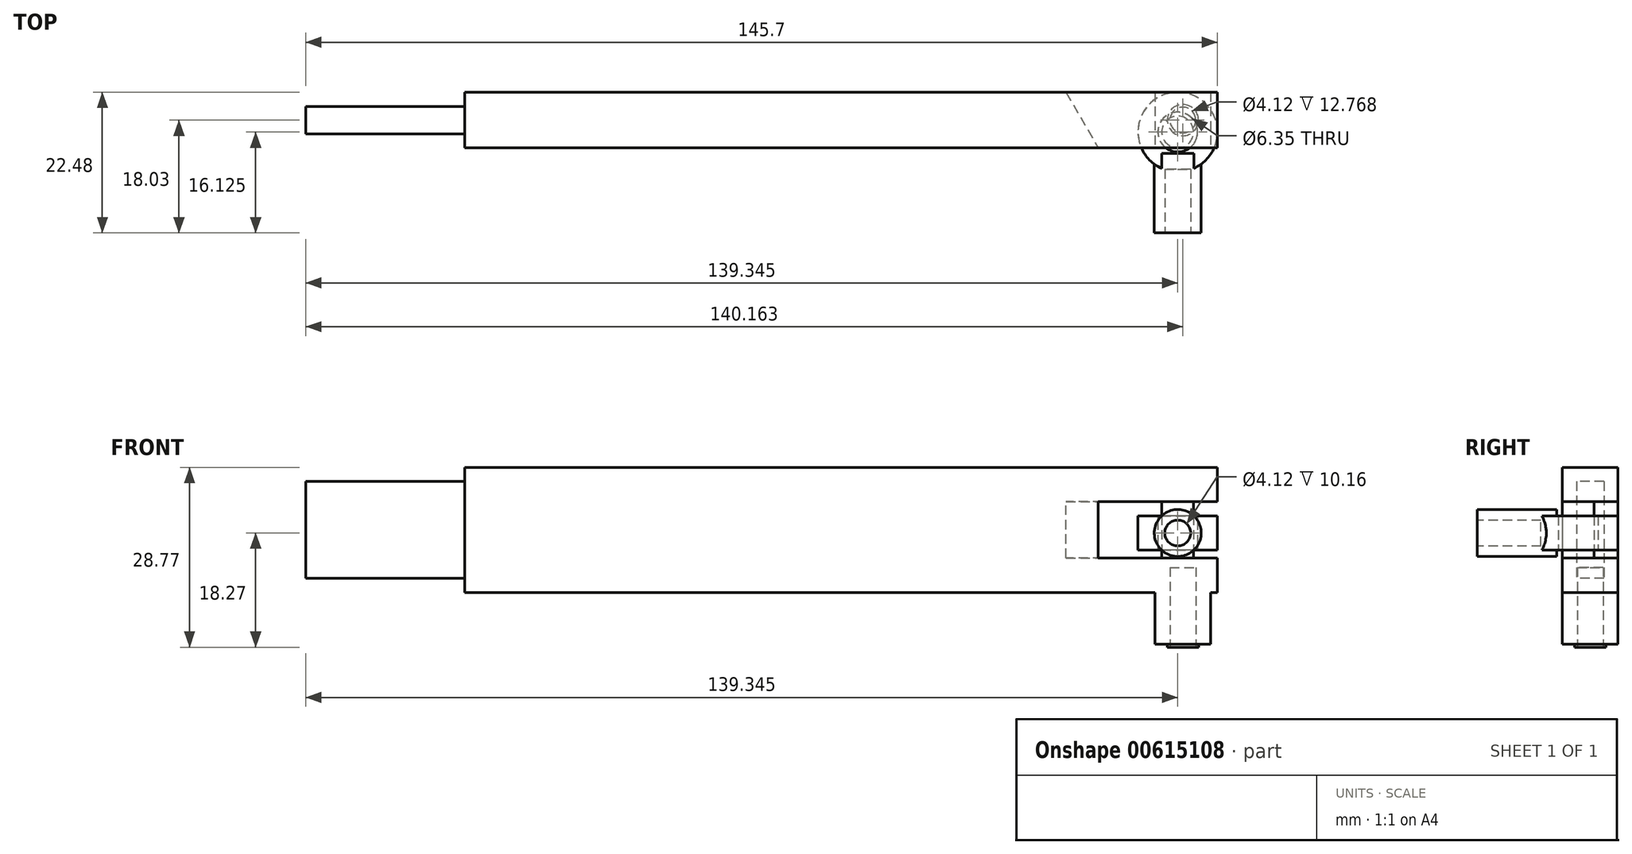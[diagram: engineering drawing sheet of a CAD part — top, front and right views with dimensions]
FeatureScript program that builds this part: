
annotation { "Feature Type Name" : "Feature", "Feature Type Description" : "" }
export const myFeature = defineFeature(function(context is Context, id is Id, definition is map)
    precondition{}
    {
        {
            var Q0;
            Q0=qCreatedBy(makeId("Top.planeOp"),FACE);
            var sketch = newSketch(context, id + "F0", { "sketchPlane" : qUnion([Q0])});
            skLineSegment(sketch, "E0.bottom", {"start": v(-60.15, 4.45) * mm, "end": v(60.15, 4.45) * mm});
            skLineSegment(sketch, "E0.top", {"start": v(-60.15, -4.44) * mm, "end": v(60.15, -4.44) * mm});
            skLineSegment(sketch, "E0.left", {"start": v(-60.15, 4.45) * mm, "end": v(-60.15, -4.44) * mm});
            skLineSegment(sketch, "E0.right", {"start": v(60.15, 4.45) * mm, "end": v(60.15, -4.44) * mm});
            skPoint(sketch, "E0.middle", {"position": v(0, 0) * mm});
            skSolve(sketch);
        }
        {
            var Q0;
            Q0=qSketchRegion(id+"F0",true);
            extrude(context, id + "F1", {"entities" : qUnion([Q0]), "endBound" : BoundingType.SYMMETRIC, "depth" : 20 * mm, "offsetDistance" : 25.4 * mm});
        }
        {
            var Q0;
            Q0=makeQuery(id+"F1.opExtrude","SWEPT_FACE",FACE,{"disambiguationData":[OSD([sQuery(id+"F0.wireOp",EDGE,"E0.left")])]});
            var sketch = newSketch(context, id + "F2", { "sketchPlane" : qUnion([Q0])});
            skLineSegment(sketch, "E1.bottom", {"start": v(-2.2, 7.75) * mm, "end": v(2.2, 7.75) * mm});
            skLineSegment(sketch, "E1.top", {"start": v(-2.2, -7.75) * mm, "end": v(2.2, -7.75) * mm});
            skLineSegment(sketch, "E1.left", {"start": v(-2.2, 7.75) * mm, "end": v(-2.2, -7.75) * mm});
            skLineSegment(sketch, "E1.right", {"start": v(2.2, 7.75) * mm, "end": v(2.2, -7.75) * mm});
            skPoint(sketch, "E1.middle", {"position": v(0, 0) * mm});
            skSolve(sketch);
        }
        {
            var Q0;
            Q0=qSketchRegion(id+"F2",true);
            extrude(context, id + "F3", {"entities" : qUnion([Q0]), "operationType" : NewBodyOperationType.ADD, "depth" : 25.4 * mm, "offsetDistance" : 25.4 * mm});
        }
        {
            var Q0;
            Q0=makeQuery(id+"F1.opExtrude","SWEPT_FACE",FACE,{"disambiguationData":[OSD([sQuery(id+"F0.wireOp",EDGE,"E0.top")])]});
            var sketch = newSketch(context, id + "F4", { "sketchPlane" : qUnion([Q0])});
            skLineSegment(sketch, "E2.bottom", {"start": v(41.1, 4.5) * mm, "end": v(60.15, 4.5) * mm});
            skLineSegment(sketch, "E2.top", {"start": v(41.1, -4.5) * mm, "end": v(60.15, -4.5) * mm});
            skLineSegment(sketch, "E2.left", {"start": v(41.1, 4.5) * mm, "end": v(41.1, -4.5) * mm});
            skLineSegment(sketch, "E2.right", {"start": v(60.15, 4.5) * mm, "end": v(60.15, -4.5) * mm});
            skPoint(sketch, "E2.middle", {"position": v(50.62, 0) * mm});
            skSolve(sketch);
        }
        {
            var Q0;
            Q0=qSketchRegion(id+"F4",true);
            extrude(context, id + "F5", {"entities" : qUnion([Q0]), "operationType" : NewBodyOperationType.REMOVE, "endBound" : BoundingType.THROUGH_ALL, "oppositeDirection" : true, "depth" : 25.4 * mm, "offsetDistance" : 25.4 * mm});
        }
        {
            var Q0;
            Q0=makeQuery(id+"F5.boolean.opBoolean","COPY",FACE,{"derivedFrom":makeQuery(id+"F5.opExtrude","SWEPT_FACE",FACE,{"disambiguationData":[OSD([sQuery(id+"F4.wireOp",EDGE,"E2.top")])]})});
            var sketch = newSketch(context, id + "F6", { "sketchPlane" : qUnion([Q0])});
            skCircle(sketch, "E3", {"center": v(53.8, -1.9) * mm, "radius": 2.54 * mm});
            skSolve(sketch);
        }
        {
            var Q0;
            Q0=qSketchRegion(id+"F6",true);
            extrude(context, id + "F7", {"entities" : qUnion([Q0]), "operationType" : NewBodyOperationType.ADD, "endBound" : BoundingType.UP_TO_NEXT, "depth" : 25.4 * mm, "offsetDistance" : 25.4 * mm});
        }
        {
            var Q0;
            Q0=makeQuery(id+"F5.boolean.opBoolean","COPY",FACE,{"derivedFrom":makeQuery(id+"F5.opExtrude","SWEPT_FACE",FACE,{"disambiguationData":[OSD([sQuery(id+"F4.wireOp",EDGE,"E2.top")])]})});
            cPlane(context, id + "F8", {"entities" : qUnion([Q0]), "cplaneType" : CPlaneType.OFFSET, "offset" : 1.27 * mm, "width" : 152.4 * mm, "height" : 152.4 * mm});
        }
        {
            var Q0;
            Q0=qCreatedBy(id+"F8.planeOp",FACE);
            var sketch = newSketch(context, id + "F9", { "sketchPlane" : qUnion([Q0])});
            skCircle(sketch, "E4.0", {"center": v(53.8, -1.9) * mm, "radius": 2.54 * mm});
            skCircle(sketch, "E5", {"center": v(53.8, -1.9) * mm, "radius": 3.17 * mm});
            skLineSegment(sketch, "E6.0", {"start": v(60.15, 4.45) * mm, "end": v(41.1, 4.45) * mm});
            skCircle(sketch, "E7", {"center": v(53.8, -1.9) * mm, "radius": 6.35 * mm});
            skSolve(sketch);
        }
        {
            var Q0;
            Q0=qSketchRegion(id+"F9",true);
            extrude(context, id + "F10", {"entities" : qUnion([Q0]), "depth" : 8 * mm - 2.54 * mm, "offsetDistance" : 25.4 * mm});
        }
        {
            var Q0;
            Q0=makeQuery(id+"F1.opExtrude","SWEPT_FACE",FACE,{"disambiguationData":[OSD([sQuery(id+"F0.wireOp",EDGE,"E0.top")])]});
            cPlane(context, id + "F11", {"entities" : qUnion([Q0]), "cplaneType" : CPlaneType.OFFSET, "offset" : 0.89 * mm, "width" : 152.4 * mm, "height" : 152.4 * mm});
        }
        {
            var Q0;
            Q0=qCreatedBy(id+"F11.planeOp",FACE);
            var sketch = newSketch(context, id + "F12", { "sketchPlane" : qUnion([Q0])});
            skLineSegment(sketch, "E8.0.0", {"start": v(60.15, -3.23) * mm, "end": v(47.45, -3.23) * mm});
            skLineSegment(sketch, "E9.0.0", {"start": v(47.45, 2.23) * mm, "end": v(60.15, 2.23) * mm});
            skLineSegment(sketch, "E10", {"start": v(53.8, 2.23) * mm, "end": v(53.8, -3.23) * mm, "construction": true});
            skCircle(sketch, "E11", {"center": v(53.8, -0.5) * mm, "radius": 3.75 * mm});
            skSolve(sketch);
        }
        {
            var Q0;
            Q0=qSketchRegion(id+"F12",true);
            extrude(context, id + "F13", {"entities" : qUnion([Q0]), "operationType" : NewBodyOperationType.ADD, "depth" : 12.7 * mm, "offsetDistance" : 25.4 * mm});
        }
        {
            var Q0;
            Q0=makeQuery(id+"F13.opExtrude","CAP_FACE",FACE,{"disambiguationData":[OSD([sQuery(id+"F12.wireOp",EDGE,"E11")])],"isStart":false});
            var sketch = newSketch(context, id + "F14", { "sketchPlane" : qUnion([Q0])});
            skCircle(sketch, "E12.0", {"center": v(53.8, -0.5) * mm, "radius": 3.75 * mm, "construction": true});
            skCircle(sketch, "E13", {"center": v(53.8, -0.5) * mm, "radius": 2.06 * mm});
            skSolve(sketch);
        }
        {
            var Q0;
            Q0=qSketchRegion(id+"F14",true);
            extrude(context, id + "F15", {"entities" : qUnion([Q0]), "operationType" : NewBodyOperationType.REMOVE, "oppositeDirection" : true, "depth" : 10.16 * mm, "offsetDistance" : 25.4 * mm});
        }
        {
            var Q0;
            Q0=makeQuery(id+"F1.opExtrude","CAP_FACE",FACE,{"disambiguationData":[OSD([sQuery(id+"F0.wireOp",EDGE,"E0.bottom"),sQuery(id+"F0.wireOp",EDGE,"E0.top"),sQuery(id+"F0.wireOp",EDGE,"E0.left"),sQuery(id+"F0.wireOp",EDGE,"E0.right")])],"isStart":true});
            var sketch = newSketch(context, id + "F16", { "sketchPlane" : qUnion([Q0])});
            skCircle(sketch, "E14", {"center": v(54.61, 0) * mm, "radius": 2.06 * mm});
            skSolve(sketch);
        }
        {
            var Q0;
            Q0 = qSketchRegion(id + "F16", true);
            extrude(context, id + "F17", {"entities" : qUnion([Q0]), "operationType" : NewBodyOperationType.REMOVE, "oppositeDirection" : true, "depth" : 4 * mm, "offsetDistance" : 25.4 * mm});
        }
        {
            var Q0;
            Q0=makeQuery(id+"F1.opExtrude","CAP_FACE",FACE,{"disambiguationData":[OSD([sQuery(id+"F0.wireOp",EDGE,"E0.bottom"),sQuery(id+"F0.wireOp",EDGE,"E0.top"),sQuery(id+"F0.wireOp",EDGE,"E0.left"),sQuery(id+"F0.wireOp",EDGE,"E0.right")])],"isStart":true});
            var sketch = newSketch(context, id + "F18", { "sketchPlane" : qUnion([Q0])});
            skCircle(sketch, "E15.0", {"center": v(54.61, 0) * mm, "radius": 2.06 * mm});
            skCircle(sketch, "E16", {"center": v(54.61, 0) * mm, "radius": 4.45 * mm});
            skLineSegment(sketch, "E17.bottom", {"start": v(50.17, -4.45) * mm, "end": v(59.06, -4.45) * mm});
            skLineSegment(sketch, "E17.top", {"start": v(50.17, 4.45) * mm, "end": v(59.06, 4.45) * mm});
            skLineSegment(sketch, "E17.left", {"start": v(50.17, -4.45) * mm, "end": v(50.17, 4.45) * mm});
            skLineSegment(sketch, "E17.right", {"start": v(59.06, -4.45) * mm, "end": v(59.06, 4.45) * mm});
            skSolve(sketch);
        }
        {
            var Q0;
            Q0 = qSketchRegion(id + "F18", true);
            extrude(context, id + "F19", {"entities" : qUnion([Q0]), "operationType" : NewBodyOperationType.ADD, "depth" : 4 * mm + 4.27 * mm, "offsetDistance" : 25.4 * mm});
        }
        {
            var Q0;
            Q0=makeQuery(id+"F19.opExtrude","CAP_FACE",FACE,{"disambiguationData":[OSD([sQuery(id+"F18.wireOp",EDGE,"E15.0"),sQuery(id+"F18.wireOp",EDGE,"E17.bottom"),sQuery(id+"F18.wireOp",EDGE,"E17.top"),sQuery(id+"F18.wireOp",EDGE,"E17.left"),sQuery(id+"F18.wireOp",EDGE,"E17.right")])],"isStart":false});
            var sketch = newSketch(context, id + "F20", { "sketchPlane" : qUnion([Q0])});
            skCircle(sketch, "E18.0", {"center": v(54.61, 0) * mm, "radius": 2.06 * mm});
            skCircle(sketch, "E19", {"center": v(54.61, 0) * mm, "radius": 2.5 * mm});
            skSolve(sketch);
        }
        {
            var Q0;
            Q0=makeQuery(id+"F20.imprint","IMPRINT",FACE,{"disambiguationData":[TD([[makeQuery(id+"F20.imprint","IMPRINT",EDGE,{"derivedFrom":sQuery(id+"F20.wireOp",EDGE,"E18.0")}),-1.0]])]});
            extrude(context, id + "F21", {"entities" : qUnion([Q0]), "operationType" : NewBodyOperationType.ADD, "depth" : .5 * mm, "offsetDistance" : 25.4 * mm});
        }
        {
            var Q0;
            Q0=makeQuery(id+"F5.boolean.opBoolean","COPY",FACE,{"derivedFrom":makeQuery(id+"F5.opExtrude","SWEPT_FACE",FACE,{"disambiguationData":[OSD([sQuery(id+"F4.wireOp",EDGE,"E2.bottom")])]})});
            var sketch = newSketch(context, id + "F22", { "sketchPlane" : qUnion([Q0])});
            skLineSegment(sketch, "E20", {"start": v(41.1, 4.44) * mm, "end": v(41.1, -4.45) * mm});
            skLineSegment(sketch, "E21", {"start": v(41.1, -4.45) * mm, "end": v(35.96, -4.45) * mm});
            skLineSegment(sketch, "E22", {"start": v(35.96, -4.45) * mm, "end": v(41.1, 4.44) * mm});
            skSolve(sketch);
        }
        {
            var Q0;
            Q0 = qSketchRegion(id + "F22", true);
            extrude(context, id + "F23", {"entities" : qUnion([Q0]), "operationType" : NewBodyOperationType.REMOVE, "depth" : 9 * mm, "offsetDistance" : 25.4 * mm});
        }
    });
